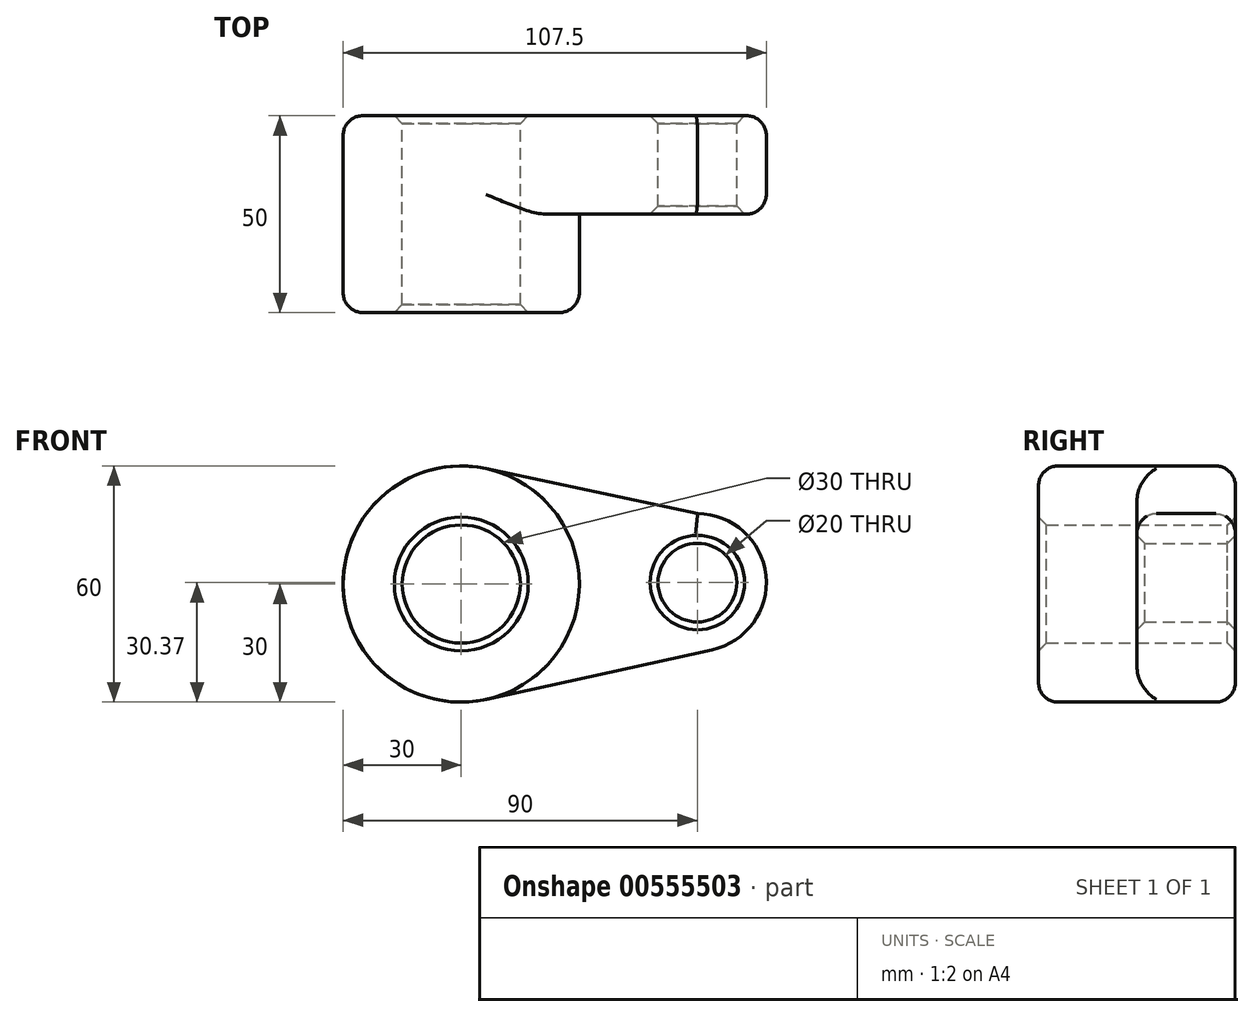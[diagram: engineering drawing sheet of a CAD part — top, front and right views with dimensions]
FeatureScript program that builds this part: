
annotation { "Feature Type Name" : "Feature", "Feature Type Description" : "" }
export const myFeature = defineFeature(function(context is Context, id is Id, definition is map)
    precondition{}
    {
        {
            var Q0;
            Q0=qCreatedBy(makeId("Front.planeOp"),FACE);
            var sketch = newSketch(context, id + "F0", { "sketchPlane" : qUnion([Q0])});
            skCircle(sketch, "E0", {"center": v(0, 0) * mm, "radius": 30 * mm});
            skCircle(sketch, "E1", {"center": v(60, 0.37) * mm, "radius": 17.5 * mm});
            skLineSegment(sketch, "E2", {"start": v(6.25, 29.34) * mm, "end": v(67.08, 16.38) * mm});
            skLineSegment(sketch, "E3", {"start": v(6.43, -29.3) * mm, "end": v(63.75, -16.72) * mm});
            skCircle(sketch, "E4", {"center": v(0, 0) * mm, "radius": 15 * mm});
            skCircle(sketch, "E5", {"center": v(60, 0.37) * mm, "radius": 10 * mm});
            skSolve(sketch);
        }
        {
            var Q0;
            Q0 = qSketchRegion(id + "F0", true);
            extrude(context, id + "F1", {"entities" : qUnion([Q0]), "depth" : 25 * mm, "offsetDistance" : 25 * mm});
        }
        {
            var Q0;
            Q0=makeQuery(id+"F0.imprint","IMPRINT",FACE,{"disambiguationData":[TD([[makeQuery(id+"F0.imprint","IMPRINT",EDGE,{"derivedFrom":sQuery(id+"F0.wireOp",EDGE,"E4")}),-1.0]])]});
            extrude(context, id + "F2", {"entities" : qUnion([Q0]), "operationType" : NewBodyOperationType.ADD, "depth" : 50 * mm, "offsetDistance" : 25 * mm});
        }
        {
            var Q0;
            Q0=makeQuery(id+"F2.opExtrude","CAP_EDGE",EDGE,{"disambiguationData":[OSD([sQuery(id+"F0.wireOp",EDGE,"E0")])],"isStart":false});
            var Q1;
            Q1=makeQuery(id+"F1.opExtrude","CAP_EDGE",EDGE,{"disambiguationData":[OSD([sQuery(id+"F0.wireOp",EDGE,"E3")])],"isStart":false});
            var Q2;
            Q2=makeQuery(id+"F1.opExtrude","CAP_EDGE",EDGE,{"disambiguationData":[OSD([sQuery(id+"F0.wireOp",EDGE,"E1")])],"isStart":false});
            var Q3;
            Q3=makeQuery(id+"F1.opExtrude","CAP_EDGE",EDGE,{"disambiguationData":[OSD([sQuery(id+"F0.wireOp",EDGE,"E2")])],"isStart":false});
            var Q4;
            Q4=makeQuery(id+"F1.opExtrude","CAP_EDGE",EDGE,{"disambiguationData":[OSD([sQuery(id+"F0.wireOp",EDGE,"E3")])],"isStart":true});
            var Q5;
            Q5=makeQuery(id+"F1.opExtrude","CAP_EDGE",EDGE,{"disambiguationData":[OSD([sQuery(id+"F0.wireOp",EDGE,"E1")])],"isStart":true});
            var Q6;
            Q6=makeQuery(id+"F1.opExtrude","CAP_EDGE",EDGE,{"disambiguationData":[OSD([sQuery(id+"F0.wireOp",EDGE,"E0")])],"isStart":true});
            var Q7;
            Q7=makeQuery(id+"F1.opExtrude","CAP_EDGE",EDGE,{"disambiguationData":[OSD([sQuery(id+"F0.wireOp",EDGE,"E2")])],"isStart":true});
            fillet(context, id + "F3", {"entities" : qUnion([Q0, Q1, Q2, Q3, Q4, Q5, Q6, Q7]), "radius" : 5 * mm, "tangentPropagation" : true, "allowEdgeOverflow" : false});
        }
        {
            var Q0;
            Q0=makeQuery(id+"F2.opExtrude","CAP_EDGE",EDGE,{"disambiguationData":[OSD([sQuery(id+"F0.wireOp",EDGE,"E4")])],"isStart":false});
            var Q1;
            Q1=makeQuery(id+"F1.opExtrude","CAP_EDGE",EDGE,{"disambiguationData":[OSD([sQuery(id+"F0.wireOp",EDGE,"E5")])],"isStart":false});
            var Q2;
            Q2=makeQuery(id+"F1.opExtrude","CAP_EDGE",EDGE,{"disambiguationData":[OSD([sQuery(id+"F0.wireOp",EDGE,"E4")])],"isStart":true});
            var Q3;
            {var subQ0=sQuery(id+"F0.wireOp",EDGE,"E1");Q3=makeQuery(id+"F3.opFillet","BLEND_EDGE",EDGE,{"blendedFrom":[makeQuery(id+"F1.opExtrude","CAP_EDGE",EDGE,{"disambiguationData":[OSD([subQ0])],"isStart":true}),makeQuery(id+"F1.opExtrude","CAP_FACE",FACE,{"disambiguationData":[OSD([sQuery(id+"F0.wireOp",EDGE,"E0"),subQ0,sQuery(id+"F0.wireOp",EDGE,"E2"),sQuery(id+"F0.wireOp",EDGE,"E3"),sQuery(id+"F0.wireOp",EDGE,"E4"),sQuery(id+"F0.wireOp",EDGE,"E5")])],"isStart":true})],"blendedInto":[makeQuery(id+"F1.opExtrude","CAP_FACE",FACE,{"disambiguationData":[OSD([sQuery(id+"F0.wireOp",EDGE,"E0"),subQ0,sQuery(id+"F0.wireOp",EDGE,"E2"),sQuery(id+"F0.wireOp",EDGE,"E3"),sQuery(id+"F0.wireOp",EDGE,"E4"),sQuery(id+"F0.wireOp",EDGE,"E5")])],"isStart":true})]});}
            var Q4;
            Q4=makeQuery(id+"F1.opExtrude","CAP_EDGE",EDGE,{"disambiguationData":[OSD([sQuery(id+"F0.wireOp",EDGE,"E5")])],"isStart":true});
            chamfer(context, id + "F4", {"entities" : qUnion([Q0, Q1, Q2, Q3, Q4]), "width" : 2 * mm, "tangentPropagation" : true});
        }
    });
